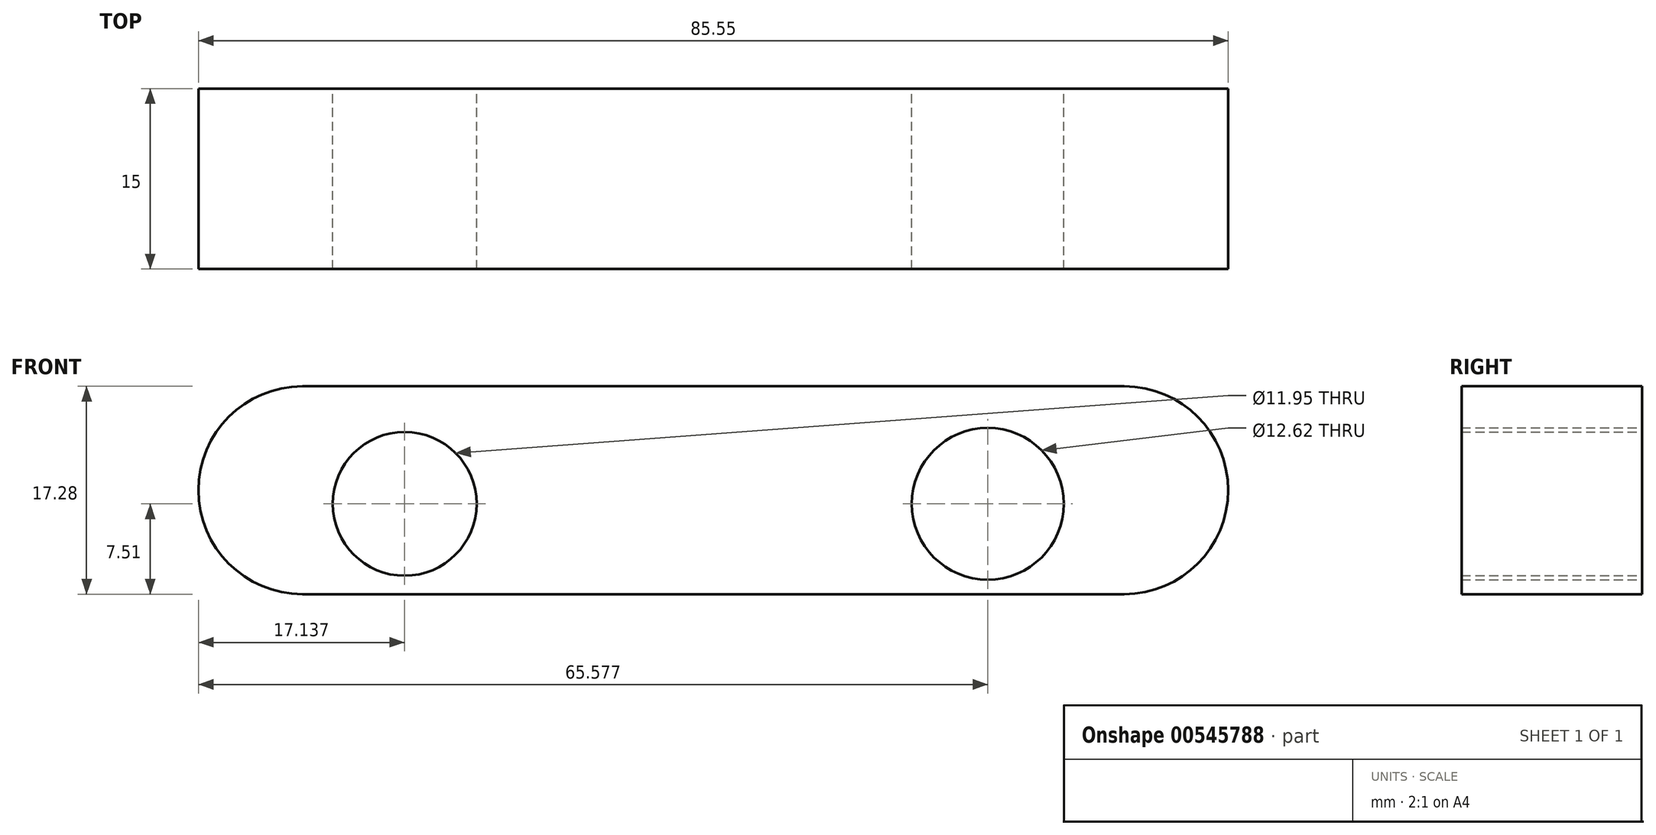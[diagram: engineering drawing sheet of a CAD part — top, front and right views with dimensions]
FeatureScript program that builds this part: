
annotation { "Feature Type Name" : "Feature", "Feature Type Description" : "" }
export const myFeature = defineFeature(function(context is Context, id is Id, definition is map)
    precondition{}
    {
        {
            var Q0;
            Q0=qCreatedBy(makeId("Front.planeOp"),FACE);
            var sketch = newSketch(context, id + "F0", { "sketchPlane" : qUnion([Q0])});
            skLineSegment(sketch, "E0", {"start": v(0, 9.77) * mm, "end": v(33.57, 9.77) * mm});
            skLineSegment(sketch, "E1", {"start": v(0, 9.77) * mm, "end": v(-34.7, 9.77) * mm});
            skLineSegment(sketch, "E2", {"start": v(-34.7, 9.77) * mm, "end": v(-34.7, -7.5) * mm});
            skLineSegment(sketch, "E3", {"start": v(-34.7, -7.5) * mm, "end": v(33.57, -7.5) * mm});
            skLineSegment(sketch, "E4", {"start": v(33.57, -7.5) * mm, "end": v(33.57, 9.77) * mm});
            skArc(sketch, "E5", {"start": v(33.57, 9.77) * mm, "mid": v(42.2, 1.13) * mm, "end": v(33.57, -7.5) * mm});
            skArc(sketch, "E6", {"start": v(-34.7, 9.77) * mm, "mid": v(-43.34, 1.13) * mm, "end": v(-34.7, -7.5) * mm});
            skCircle(sketch, "E7", {"center": v(-26.2, 0) * mm, "radius": 5.98 * mm});
            skCircle(sketch, "E8", {"center": v(22.24, 0) * mm, "radius": 6.31 * mm});
            skSolve(sketch);
        }
        {
            var Q0;
            Q0=makeQuery(id+"F0.imprint","IMPRINT",FACE,{"disambiguationData":[TD([[makeQuery(id+"F0.imprint","IMPRINT",EDGE,{"derivedFrom":sQuery(id+"F0.wireOp",EDGE,"E0")}),-1.0]])]});
            var Q1;
            Q1=makeQuery(id+"F0.imprint","IMPRINT",FACE,{"disambiguationData":[TD([[makeQuery(id+"F0.imprint","IMPRINT",EDGE,{"derivedFrom":sQuery(id+"F0.wireOp",EDGE,"E2")}),-1.0]])]});
            var Q2;
            Q2=makeQuery(id+"F0.imprint","IMPRINT",FACE,{"disambiguationData":[TD([[makeQuery(id+"F0.imprint","IMPRINT",EDGE,{"derivedFrom":sQuery(id+"F0.wireOp",EDGE,"E4")}),-1.0]])]});
            extrude(context, id + "F1", {"entities" : qUnion([Q0, Q1, Q2]), "depth" : 15 * mm, "offsetDistance" : 25 * mm});
        }
    });
